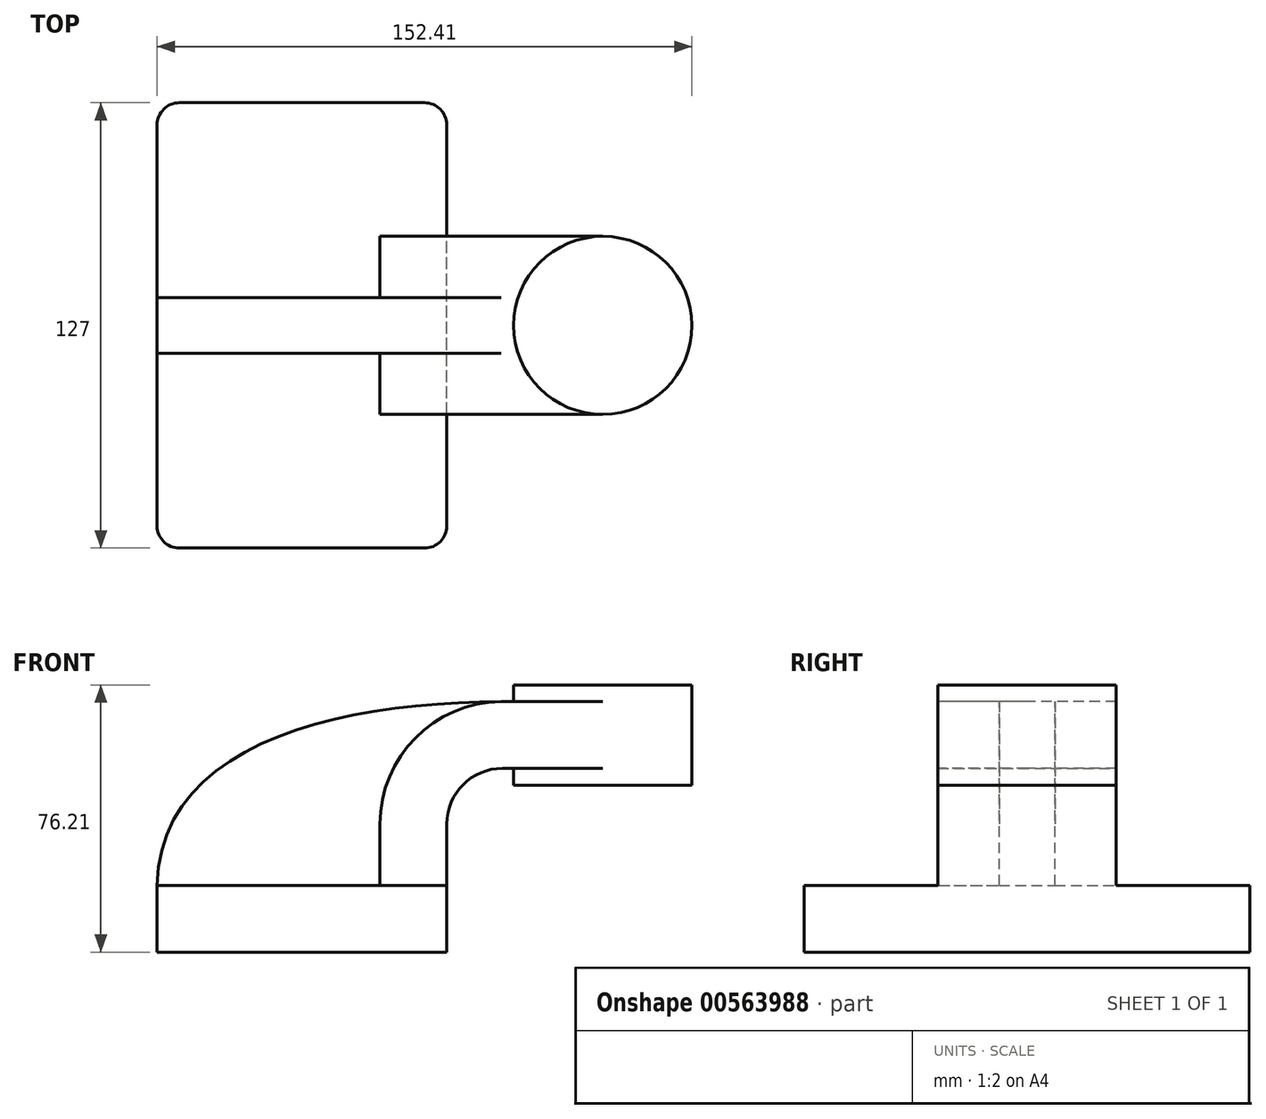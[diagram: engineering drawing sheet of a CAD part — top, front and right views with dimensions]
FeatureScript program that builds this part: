
annotation { "Feature Type Name" : "Feature", "Feature Type Description" : "" }
export const myFeature = defineFeature(function(context is Context, id is Id, definition is map)
    precondition{}
    {
        {
            var Q0;
            Q0=qCreatedBy(makeId("Front.planeOp"),FACE);
            var sketch = newSketch(context, id + "F0", { "sketchPlane" : qUnion([Q0])});
            skLineSegment(sketch, "E0.bottom", {"start": v(41.28, -9.52) * mm, "end": v(-41.28, -9.53) * mm});
            skLineSegment(sketch, "E0.top", {"start": v(41.28, 9.53) * mm, "end": v(-41.28, 9.53) * mm});
            skLineSegment(sketch, "E0.left", {"start": v(41.28, -9.52) * mm, "end": v(41.28, 9.53) * mm});
            skLineSegment(sketch, "E0.right", {"start": v(-41.28, -9.53) * mm, "end": v(-41.28, 9.53) * mm});
            skPoint(sketch, "E0.middle", {"position": v(0, 0) * mm});
            skLineSegment(sketch, "E1.bottom", {"start": v(111.12, 38.1) * mm, "end": v(60.33, 38.1) * mm});
            skLineSegment(sketch, "E1.top", {"start": v(111.12, 66.68) * mm, "end": v(60.33, 66.68) * mm});
            skLineSegment(sketch, "E1.left", {"start": v(111.12, 38.1) * mm, "end": v(111.12, 66.68) * mm});
            skLineSegment(sketch, "E1.right", {"start": v(60.33, 38.1) * mm, "end": v(60.33, 66.68) * mm});
            skPoint(sketch, "E1.middle", {"position": v(85.72, 52.39) * mm});
            skLineSegment(sketch, "E2", {"start": v(41.28, 9.53) * mm, "end": v(41.28, 27) * mm});
            skArc(sketch, "E3", {"start": v(41.27, 27) * mm, "mid": v(45.92, 38.23) * mm, "end": v(57.15, 42.88) * mm});
            skLineSegment(sketch, "E4", {"start": v(57.15, 42.88) * mm, "end": v(85.72, 42.88) * mm});
            skLineSegment(sketch, "E5.0", {"start": v(57.15, 61.93) * mm, "end": v(85.72, 61.93) * mm});
            skArc(sketch, "E5.1", {"start": v(22.23, 27) * mm, "mid": v(32.45, 51.7) * mm, "end": v(57.15, 61.93) * mm});
            skLineSegment(sketch, "E5.2", {"start": v(22.22, 9.53) * mm, "end": v(22.22, 27) * mm});
            skLineSegment(sketch, "E6", {"start": v(85.72, 38.1) * mm, "end": v(85.72, 66.68) * mm});
            skFitSpline(sketch, "E7", {"points": [v(-41.28, 9.52) * mm, v(57.15, 61.93) * mm], "startDerivative": vector(2.8, 122.56) * mm, "endDerivative": vector(139.2, 0.73) * mm});
            skSolve(sketch);
        }
        {
            var Q0;
            Q0=makeQuery(id+"F0.imprint","IMPRINT",FACE,{"disambiguationData":[TD([[makeQuery(id+"F0.imprint","IMPRINT",EDGE,{"derivedFrom":sQuery(id+"F0.wireOp",EDGE,"E0.bottom")}),-1.0]])]});
            extrude(context, id + "F1", {"entities" : qUnion([Q0]), "endBound" : BoundingType.SYMMETRIC, "depth" : 127 * mm, "offsetDistance" : 25.4 * mm});
        }
        {
            var Q0;
            {var subQ1=sQuery(id+"F0.wireOp",EDGE,"E2");Q0=makeQuery(id+"F0.imprint","IMPRINT",FACE,{"disambiguationData":[TD([[makeQuery(id+"F0.imprint","IMPRINT",EDGE,{"derivedFrom":subQ1}),1.0]])]});}
            var Q1;
            {var subQ0=sQuery(id+"F0.wireOp",EDGE,"E4");var subQ1=sQuery(id+"F0.wireOp",EDGE,"E1.right");var subQ2=makeQuery(id+"F0.imprint","INTERSECT",VERTEX,{"derivedFrom":[subQ1,subQ0]});Q1=makeQuery(id+"F0.imprint","IMPRINT",FACE,{"disambiguationData":[TD([[makeQuery(id+"F0.imprint","IMPRINT",EDGE,{"disambiguationData":[TD([[subQ2,-1.0]])],"derivedFrom":subQ1}),-1.0]])]});}
            extrude(context, id + "F2", {"entities" : qUnion([Q0, Q1]), "operationType" : NewBodyOperationType.ADD, "endBound" : BoundingType.SYMMETRIC, "depth" : 50.8 * mm, "offsetDistance" : 25.4 * mm});
        }
        {
            var Q0;
            {var subQ3=sQuery(id+"F0.wireOp",EDGE,"E5.2");Q0=makeQuery(id+"F0.imprint","IMPRINT",FACE,{"disambiguationData":[TD([[makeQuery(id+"F0.imprint","IMPRINT",EDGE,{"derivedFrom":subQ3}),1.0]])]});}
            extrude(context, id + "F3", {"entities" : qUnion([Q0]), "operationType" : NewBodyOperationType.ADD, "endBound" : BoundingType.SYMMETRIC, "depth" : 15.88 * mm, "offsetDistance" : 25.4 * mm});
        }
        {
            var Q0;
            {var subQ0=sQuery(id+"F0.wireOp",EDGE,"E1.left");Q0=makeQuery(id+"F0.imprint","IMPRINT",FACE,{"disambiguationData":[TD([[makeQuery(id+"F0.imprint","IMPRINT",EDGE,{"derivedFrom":subQ0}),1.0]])]});}
            var Q1;
            Q1=sQuery(id+"F0.wireOp",EDGE,"E6");
            revolve(context, id + "F4", {"operationType" : NewBodyOperationType.ADD, "entities" : qUnion([Q0]), "axis" : qUnion([Q1]), "revolveType" : RevolveType.FULL});
        }
        {
            var Q0;
            Q0=makeQuery(id+"F1.opExtrude","CAP_EDGE",EDGE,{"disambiguationData":[OSD([sQuery(id+"F0.wireOp",EDGE,"E0.right")])],"isStart":false});
            var Q1;
            Q1=makeQuery(id+"F1.opExtrude","CAP_EDGE",EDGE,{"disambiguationData":[OSD([sQuery(id+"F0.wireOp",EDGE,"E0.left")])],"isStart":false});
            var Q2;
            Q2=makeQuery(id+"F1.opExtrude","CAP_EDGE",EDGE,{"disambiguationData":[OSD([sQuery(id+"F0.wireOp",EDGE,"E0.left")])],"isStart":true});
            var Q3;
            Q3=makeQuery(id+"F1.opExtrude","CAP_EDGE",EDGE,{"disambiguationData":[OSD([sQuery(id+"F0.wireOp",EDGE,"E0.right")])],"isStart":true});
            fillet(context, id + "F5", {"entities" : qUnion([Q0, Q1, Q2, Q3]), "radius" : 6.35 * mm, "tangentPropagation" : true, "allowEdgeOverflow" : false});
        }
    });
